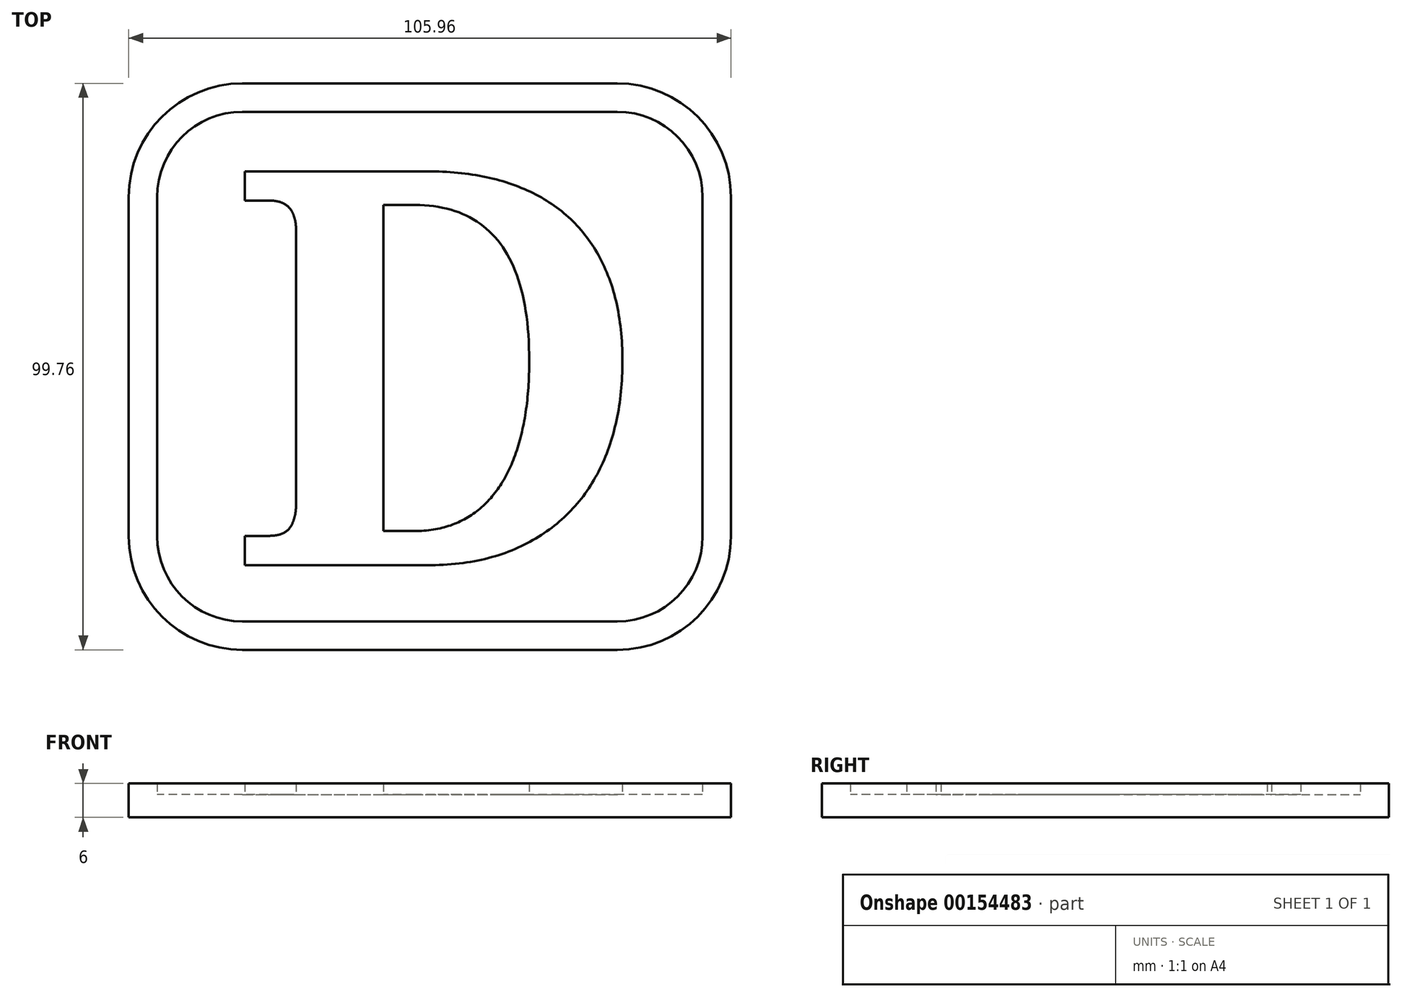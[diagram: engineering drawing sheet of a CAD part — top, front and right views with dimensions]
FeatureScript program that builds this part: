
annotation { "Feature Type Name" : "Feature", "Feature Type Description" : "" }
export const myFeature = defineFeature(function(context is Context, id is Id, definition is map)
    precondition{}
    {
        {
            var Q0;
            Q0=qCreatedBy(makeId("Top.planeOp"),FACE);
            var sketch = newSketch(context, id + "F0", { "sketchPlane" : qUnion([Q0])});
            skLineSegment(sketch, "E0.bottom", {"start": v(-32.98, 44.88) * mm, "end": v(32.98, 44.88) * mm});
            skLineSegment(sketch, "E0.top", {"start": v(-32.98, -44.88) * mm, "end": v(32.98, -44.88) * mm});
            skLineSegment(sketch, "E0.left", {"start": v(-47.98, 29.88) * mm, "end": v(-47.98, -29.88) * mm});
            skLineSegment(sketch, "E0.right", {"start": v(47.98, 29.88) * mm, "end": v(47.98, -29.88) * mm});
            skPoint(sketch, "E0.middle", {"position": v(0, 0) * mm});
            skPoint(sketch, "E1.visualSharp", {"position": v(-47.98, 44.88) * mm});
            skArc(sketch, "E1.filletArc", {"start": v(-32.98, 44.88) * mm, "mid": v(-43.59, 40.49) * mm, "end": v(-47.98, 29.88) * mm});
            skPoint(sketch, "E2.visualSharp", {"position": v(47.98, 44.88) * mm});
            skArc(sketch, "E2.filletArc", {"start": v(47.98, 29.88) * mm, "mid": v(43.59, 40.49) * mm, "end": v(32.98, 44.88) * mm});
            skPoint(sketch, "E3.visualSharp", {"position": v(47.98, -44.88) * mm});
            skArc(sketch, "E3.filletArc", {"start": v(32.98, -44.88) * mm, "mid": v(43.59, -40.49) * mm, "end": v(47.98, -29.88) * mm});
            skPoint(sketch, "E4.visualSharp", {"position": v(-47.98, -44.88) * mm});
            skArc(sketch, "E4.filletArc", {"start": v(-47.98, -29.88) * mm, "mid": v(-43.59, -40.49) * mm, "end": v(-32.98, -44.88) * mm});
            skLineSegment(sketch, "E5.0", {"start": v(-32.98, 49.88) * mm, "end": v(32.98, 49.88) * mm});
            skArc(sketch, "E5.1", {"start": v(52.98, 29.88) * mm, "mid": v(47.13, 44.02) * mm, "end": v(32.98, 49.88) * mm});
            skArc(sketch, "E5.2", {"start": v(-32.98, 49.88) * mm, "mid": v(-47.13, 44.02) * mm, "end": v(-52.98, 29.88) * mm});
            skLineSegment(sketch, "E5.3", {"start": v(52.98, 29.88) * mm, "end": v(52.98, -29.88) * mm});
            skLineSegment(sketch, "E5.4", {"start": v(-52.98, 29.88) * mm, "end": v(-52.98, -29.88) * mm});
            skArc(sketch, "E5.5", {"start": v(-52.98, -29.88) * mm, "mid": v(-47.13, -44.02) * mm, "end": v(-32.98, -49.88) * mm});
            skLineSegment(sketch, "E5.6", {"start": v(-32.98, -49.88) * mm, "end": v(32.98, -49.88) * mm});
            skArc(sketch, "E5.7", {"start": v(32.98, -49.88) * mm, "mid": v(47.13, -44.02) * mm, "end": v(52.98, -29.88) * mm});
            skSolve(sketch);
        }
        {
            var Q0;
            Q0=makeQuery(id+"F0.imprint","IMPRINT",FACE,{"disambiguationData":[TD([[makeQuery(id+"F0.imprint","IMPRINT",EDGE,{"derivedFrom":sQuery(id+"F0.wireOp",EDGE,"E0.bottom")}),-1.0]])]});
            extrude(context, id + "F1", {"entities" : qUnion([Q0]), "depth" : 4 * mm});
        }
        {
            var Q0;
            Q0=qSketchRegion(id+"F0",true);
            extrude(context, id + "F2", {"entities" : qUnion([Q0]), "operationType" : NewBodyOperationType.ADD, "depth" : 6 * mm});
        }
        {
            var Q0;
            Q0=qCreatedBy(makeId("Top.planeOp"),FACE);
            var sketch = newSketch(context, id + "F3", { "sketchPlane" : qUnion([Q0])});
            skText(sketch, "E6", { "text": "D", "fontName": "NotoSerif-Bold.ttf"});
            const initialGuessF3  = {"E6": [-0.03528, -0.03498, 1, 0, 0.06996]};
            skSetInitialGuess(sketch, initialGuessF3);
            skSolve(sketch);
        }
        {
            var Q0;
            Q0 = qSketchRegion(id + "F3", true);
            extrude(context, id + "F4", {"entities" : qUnion([Q0]), "operationType" : NewBodyOperationType.ADD, "depth" : 6 * mm});
        }
    });
